# Revit family: Lavatory-Rear_Mounted-Acorn-Penal_Ware-1659
name_source: partatom
category: Plumbing Fixtures
revit_build: Autodesk Revit 2018 (Build: 20170223_1515(x64)
units: mm (PartAtom-declared; Revit-internal decimal feet)

## family parameters
Cut with Voids When Loaded = No
Host = Face
OmniClass Number = 23.45.05.14.14
OmniClass Title = Sinks/Lavatories
Part Type = Normal
Room Calculation Point = No
Round Connector Dimension = Use Diameter
Shared = Yes

## types (1)
- 1659
    -03 Single Temp, Non-Metering = No
    -03-M Single Temp, Metering = No
    -04 Hot & Cold, Non-Metering = No
    -04-M Hot & Cold, Metering = No
    -04-MH Hot & Cold, Metering Hot Side Only = No
    -1 Off-Floor, Wall Outlet = Yes
    -9 Punched for Valve by Others = No
    -BC Bubbler, Code = No
    -BP Bubbler, Penal = Yes
    -BPH Hemispherical Penal Bubbler = No
    -BRS Brass Body Valve = No
    -CI Cycle Interrupt for Time-Trol Valves = No
    -EG Enviro-Glaze, Specify Color = No
    -EVS1 Single Temp = No
    -EVS2 Hot & Cold = No
    -EVSP1 Single Temp, Piezo Button = No
    -EVSP2 Hot & Cold, Piezo Buttons = No
    -FMT Fixture Mounted Trim = No
    -IS Integral Shelf = No
    -LF Lav-Filler = No
    -LW1 Thru-Wall Waste Extension with P-Trap = Yes
    -LWE Lavy Waste Extension (3” Standard) Specify Length Beyond Fixture = No
    -MA2 Manifolded, 2-Stack = No
    -MA3 Manifolded, 3-Stack (N/A with -PFB option) = No
    -MA4 Manifolded, 4-Stack (N/A with -PFB option) = No
    -MT Metal Template (Only 1 Required Per Project) = Yes
    -MTP1 Single Temp = No
    -MTP2 Hot & Cold = No
    -MTPP1 Single Temp, Piezo Button = No
    -MTPP2 Hot & Cold, Piezo Buttons = No
    -MVC1 Single Temp = No
    -MVC1-BAT Single Temp Battery Powered (Batteries Not Included) = No
    -MVC2 Hot & Cold = No
    -MVC2-BAT Hot & Cold Battery Powered (Batteries Not Included) = No
    -OF Lavatory Overflow = No
    -PBH Hemispherical Pushbutton = No
    -PBP Pushrod Activated Pushbutton = No
    -PFB Power Failure Bypass = No
    -PH Paper Holder Left = No
    -PH Paper Holder Right = No
    -PPZ1 Single Temp Programmable Piezo Button = No
    -PPZ2 Hot & Cold Programmable Piezo Button = No
    -PT P-Trap Waste = No
    -SW Wall Sleeve = No
    -TB Toothbrush Holder Left = No
    -TB Toothbrush Holder Right = No
    -TF Transformer, 120VAC to 24VAC (-MVC option only) = No
    -TG 12 Gage Cabinet = No
    -TH Towel Hook Left = No
    -TH Towel Hook Right = No
    -VAC AcornVac System = No
    -VG1 Vent Grille, 5-3/4" x 8-3/4" Left = No
    -VG1 Vent Grille, 5-3/4" x 8-3/4" Right = No
    -VG2 Vent Grille, 8-3/4" x 13" (Bottom Only) = No
    Assembly Code = D2010300
    Basin Shape = Multi-Sided
    CW Connection = No
    CWFU = 1.5
    Default Elevation = 32 1/2"
    Description = Rear Mount, 15 inch Compact Stainless Steel Security Lavatory with Multi-Sided Bowl
    Finish = Stainless Steel-Acorn-Satin
    HW Connection = No
    HWFU = 1.5
    Height = 14 1/2"
    Installation Type = Wall mount
    Length = 11"
    Manufacturer = Acorn
    Material = Stainless Steel-Acorn-Satin
    Model = 1659
    Price = Prices may vary. Please consult Manufacturer Representative for most up-to-date price list.
    Product Documentation Link = https://www.acorneng.com
    Product Page URL = https://www.acorneng.com
    Tempered Connection = Yes
    Tempered Water Connection Diameter = 1/2"
    Tempered Water Connection Radius = 1/4"
    URL = https://www.acorneng.com
    Vent Connection = No
    WFU = 2
    Waste Connection = Yes
    Waste Connection Diameter = 1 1/2"
    Waste Connection Height = 10 1/4"
    Waste Connection Radius = 3/4"
    Width = 15"

## geometry (parser evidence)
native form markers: Sweep x2
no freeform markers — native parametric forms only
